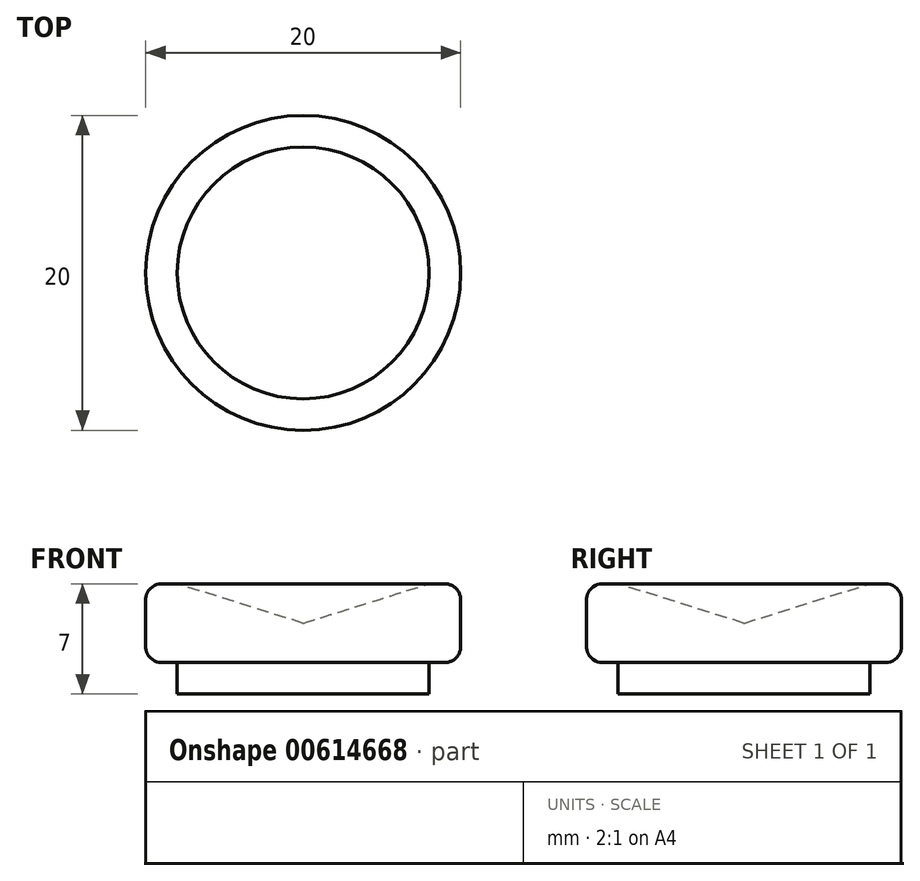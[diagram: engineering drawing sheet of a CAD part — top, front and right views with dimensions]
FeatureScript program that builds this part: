
annotation { "Feature Type Name" : "Feature", "Feature Type Description" : "" }
export const myFeature = defineFeature(function(context is Context, id is Id, definition is map)
    precondition{}
    {
        {
            var Q0;
            Q0=qCreatedBy(makeId("Top.planeOp"),FACE);
            var sketch = newSketch(context, id + "F0", { "sketchPlane" : qUnion([Q0])});
            skCircle(sketch, "E0", {"center": v(0, 0) * mm, "radius": 10 * mm});
            skSolve(sketch);
        }
        {
            var Q0;
            Q0 = qSketchRegion(id + "F0", true);
            extrude(context, id + "F1", {"entities" : qUnion([Q0]), "depth" : 5 * mm, "offsetDistance" : 25 * mm});
        }
        {
            var Q0;
            Q0=qCreatedBy(makeId("Front.planeOp"),FACE);
            var sketch = newSketch(context, id + "F2", { "sketchPlane" : qUnion([Q0])});
            skLineSegment(sketch, "E1", {"start": v(0, 2.5) * mm, "end": v(-8, 5) * mm});
            skLineSegment(sketch, "E2", {"start": v(-8, 5) * mm, "end": v(0, 5) * mm});
            skLineSegment(sketch, "E3", {"start": v(0, 5) * mm, "end": v(0, 2.5) * mm});
            skSolve(sketch);
        }
        {
            var Q0;
            Q0 = qSketchRegion(id + "F2", true);
            var Q1;
            Q1=sQuery(id+"F2.wireOp",EDGE,"E3");
            revolve(context, id + "F3", {"operationType" : NewBodyOperationType.REMOVE, "entities" : qUnion([Q0]), "axis" : qUnion([Q1]), "revolveType" : RevolveType.FULL, "oppositeDirection" : true});
        }
        {
            var Q0;
            Q0=makeQuery(id+"F1.opExtrude","CAP_FACE",FACE,{"disambiguationData":[OSD([sQuery(id+"F0.wireOp",EDGE,"E0")])],"isStart":true});
            var sketch = newSketch(context, id + "F4", { "sketchPlane" : qUnion([Q0])});
            skCircle(sketch, "E4", {"center": v(0, 0) * mm, "radius": 8 * mm});
            skSolve(sketch);
        }
        {
            var Q0;
            Q0 = qSketchRegion(id + "F4", true);
            extrude(context, id + "F5", {"entities" : qUnion([Q0]), "operationType" : NewBodyOperationType.ADD, "depth" : 2 * mm, "offsetDistance" : 25 * mm});
        }
        {
            var Q0;
            Q0=makeQuery(id+"F5.opExtrude","CAP_EDGE",EDGE,{"disambiguationData":[OSD([sQuery(id+"F4.wireOp",EDGE,"E4")])],"isStart":true});
            var Q1;
            Q1=makeQuery(id+"F1.opExtrude","CAP_EDGE",EDGE,{"disambiguationData":[OSD([sQuery(id+"F0.wireOp",EDGE,"E0")])],"isStart":true});
            var Q2;
            Q2=makeQuery(id+"F1.opExtrude","CAP_EDGE",EDGE,{"disambiguationData":[OSD([sQuery(id+"F0.wireOp",EDGE,"E0")])],"isStart":false});
            var Q3;
            Q3=makeQuery(id+"F3.boolean.opBoolean","COPY",EDGE,{"derivedFrom":makeQuery(id+"F3.opRevolve","SWEPT_EDGE",EDGE,{"disambiguationData":[OSD([sQuery(id+"F2.wireOp",EDGE,"E1"),sQuery(id+"F2.wireOp",EDGE,"E2")])]})});
            fillet(context, id + "F6", {"entities" : qUnion([Q0, Q1, Q2, Q3]), "radius" : 1 * mm, "tangentPropagation" : true, "allowEdgeOverflow" : false});
        }
    });
